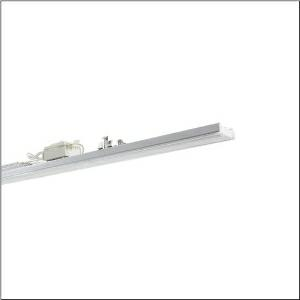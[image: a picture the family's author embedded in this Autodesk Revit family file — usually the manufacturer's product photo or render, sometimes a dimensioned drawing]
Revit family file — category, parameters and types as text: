
# Revit family: licross_r__21_recessed_ho_51te11vn4c5s_561a
name_source: partatom
category: Lighting Fixtures
units: mm (PartAtom-declared; Revit-internal decimal feet)

## family parameters
Cut with Voids When Loaded = No
Host = Face
Light Source = No
Part Type = Normal
Room Calculation Point = No
Round Connector Dimension = Use Diameter
Shared = No

## types (1)
- --- (1 x LED, 12960 lm, 70.6 W, 4000K)
    Apparent Load = 71 VA
    CIE Flux Codes = 84 94 98 99 100
    Color Rendering = 80
    Color Temperature = 4000K
    Default Elevation = 1800 mm
    Description = Licross® 21 Recessed HO, luminaire insert, of sheet steel, galvanised, coil coated, white, length: 1.500mm, width: 66mm, height: 67mm, LED rated luminous flux: 12.960lm, light colour: 840, control gear: DALI 2, CLO, with plug, 5-pole, with phase selection, mains connection: 220..240V, AC, 50/60Hz, start of lifetime: 71W, end of service life: 77W, internal wiring halogen-free, primary optical cover: cover, of PMMA, light emission: direct distribution, primary light characteristic: symmetric, protection rating (complete): IP54, insulation class (complete): insulation class I (protective earthing), certification: CE, ENEC, VDE, UKCA, protection symbol: D if used in an environment with non-conductive dust loads with corresponding accessories, impact resistance: IK06, permissible ambient temperature for indoor applications: -25..+35°C, corresponds to IFS (International Featured Standards) requirements for safety and quality in the food industry, reducing of maximum allowable ambient temperature of 5°C with ceiling mounting, LABS conformity tested according to VDMA 24364:2018-05, packaging unit: 1 piece
    Height = 58 mm
    Lamp = 1 x LED
    Lamp Light Flux = 12960 lm
    Lamp Power = 70.6 W
    Lamp count = 1
    Length = 1500 mm
    Luminous efficacy = 184 lm/W
    Manufacturer = Siteco
    ModVariant = No
    Model = 51TE11VN4C5S
    Mounting Place = Ceiling
    Mounting Type = Pendant
    Number of Poles = 1
    OnlyDefault = Yes
    Power Factor = 1
    Product Name = Licross® 21 Recessed HO
    Product group = luminaire insert | ceiling pendant
    ProductGroupID = 902
    Protection Class = Protection class I
    Protection Degree = IP 54
    RLX_Detail_Level = 1
    RLX_Emergency_Light_Flux = 0 lm
    RLX_Emergency_Type = 0
    RLX_Emergency_Type_DB = No
    RlxData = <blob elided: 24937 chars, md5=73545641>
    Socket = socket
    Standby Power = 0 W
    System Light Flux = 12960 lm
    System Power = 71 W
    Type Comments = factory setting: luminous flux: 100 % | dim-lin: 254 | 480 mA
    Type Image = l_1296930.jpg
    URL = http://relux.com
    VarID = @adj_069765
    Voltage = 0 V
    Weight = 0.00 kg
    Width = 66 mm

## geometry (parser evidence)
native form markers: Blend x4, Sweep x9
no freeform markers — native parametric forms only
